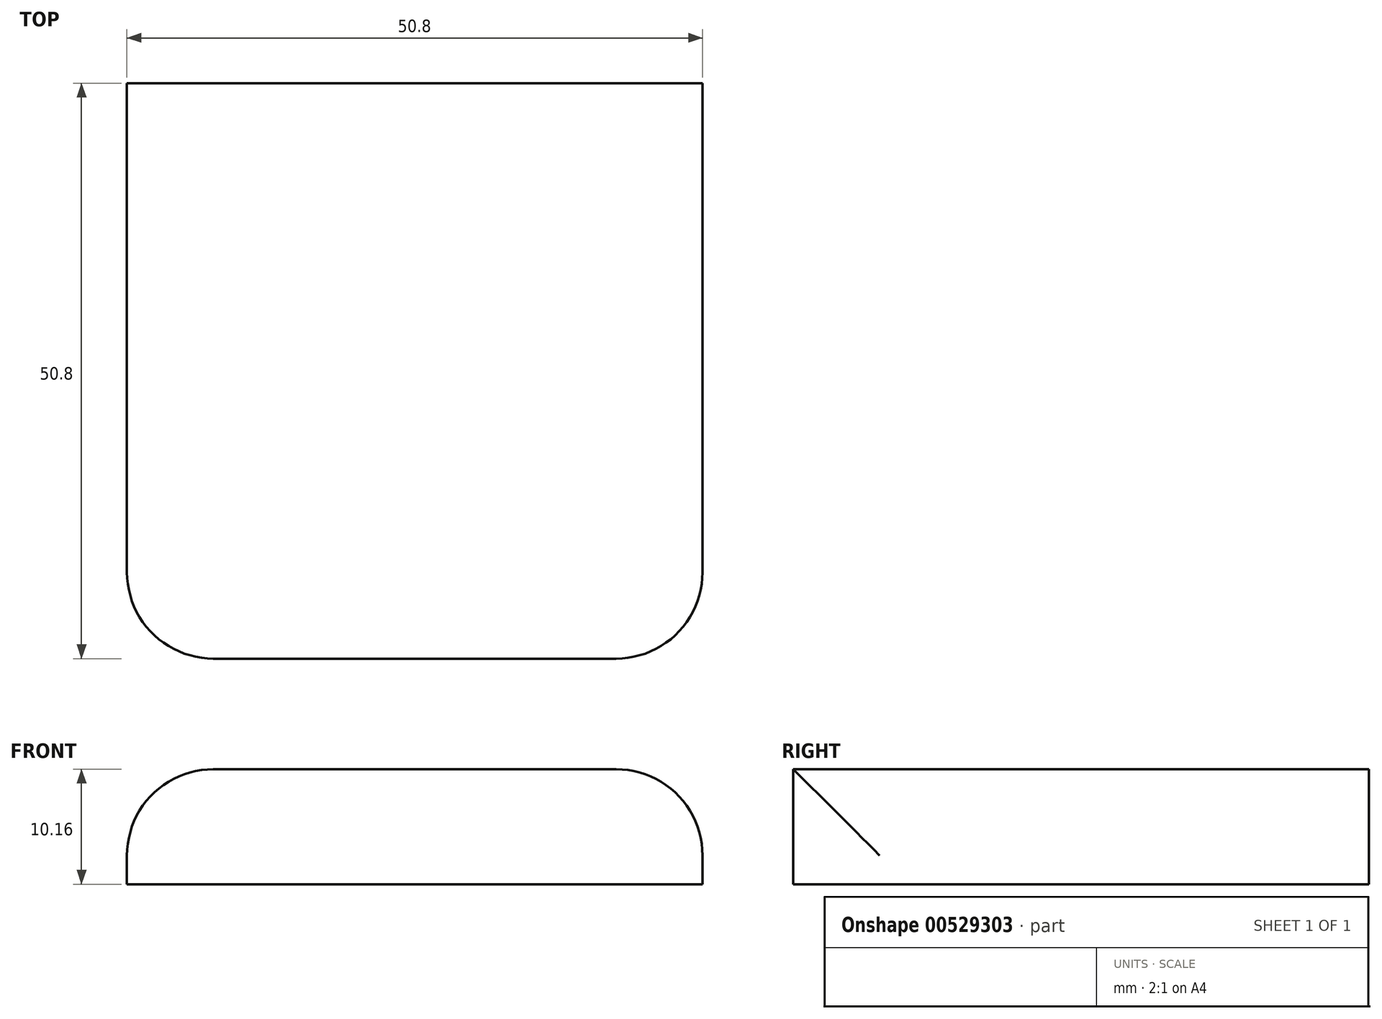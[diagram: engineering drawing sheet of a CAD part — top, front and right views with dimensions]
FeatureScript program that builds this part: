
annotation { "Feature Type Name" : "Feature", "Feature Type Description" : "" }
export const myFeature = defineFeature(function(context is Context, id is Id, definition is map)
    precondition{}
    {
        {
            var Q0;
            Q0=qCreatedBy(makeId("Top.planeOp"),FACE);
            var sketch = newSketch(context, id + "F0", { "sketchPlane" : qUnion([Q0])});
            skLineSegment(sketch, "E0.bottom", {"start": v(0, 0) * mm, "end": v(50.8, 0) * mm});
            skLineSegment(sketch, "E0.top", {"start": v(0, -50.8) * mm, "end": v(50.8, -50.8) * mm});
            skLineSegment(sketch, "E0.left", {"start": v(0, 0) * mm, "end": v(0, -50.8) * mm});
            skLineSegment(sketch, "E0.right", {"start": v(50.8, 0) * mm, "end": v(50.8, -50.8) * mm});
            skSolve(sketch);
        }
        {
            var Q0;
            Q0=makeQuery(id+"F0.imprint","IMPRINT",FACE,{"disambiguationData":[TD([[makeQuery(id+"F0.imprint","IMPRINT",EDGE,{"derivedFrom":sQuery(id+"F0.wireOp",EDGE,"E0.bottom")}),-1.0]])]});
            extrude(context, id + "F1", {"entities" : qUnion([Q0]), "depth" : 10.16 * mm, "offsetDistance" : 25.4 * mm});
        }
        {
            var Q0;
            Q0=makeQuery(id+"F1.opExtrude","SWEPT_EDGE",EDGE,{"disambiguationData":[OSD([sQuery(id+"F0.wireOp",EDGE,"E0.top"),sQuery(id+"F0.wireOp",EDGE,"E0.right")])]});
            var Q1;
            Q1=makeQuery(id+"F1.opExtrude","SWEPT_EDGE",EDGE,{"disambiguationData":[OSD([sQuery(id+"F0.wireOp",EDGE,"E0.top"),sQuery(id+"F0.wireOp",EDGE,"E0.left")])]});
            var Q2;
            Q2=makeQuery(id+"F1.opExtrude","CAP_EDGE",EDGE,{"disambiguationData":[OSD([sQuery(id+"F0.wireOp",EDGE,"E0.left")])],"isStart":false});
            var Q3;
            Q3=makeQuery(id+"F1.opExtrude","CAP_EDGE",EDGE,{"disambiguationData":[OSD([sQuery(id+"F0.wireOp",EDGE,"E0.right")])],"isStart":false});
            fillet(context, id + "F2", {"entities" : qUnion([Q0, Q1, Q2, Q3]), "radius" : 7.62 * mm, "tangentPropagation" : true, "allowEdgeOverflow" : false});
        }
    });
